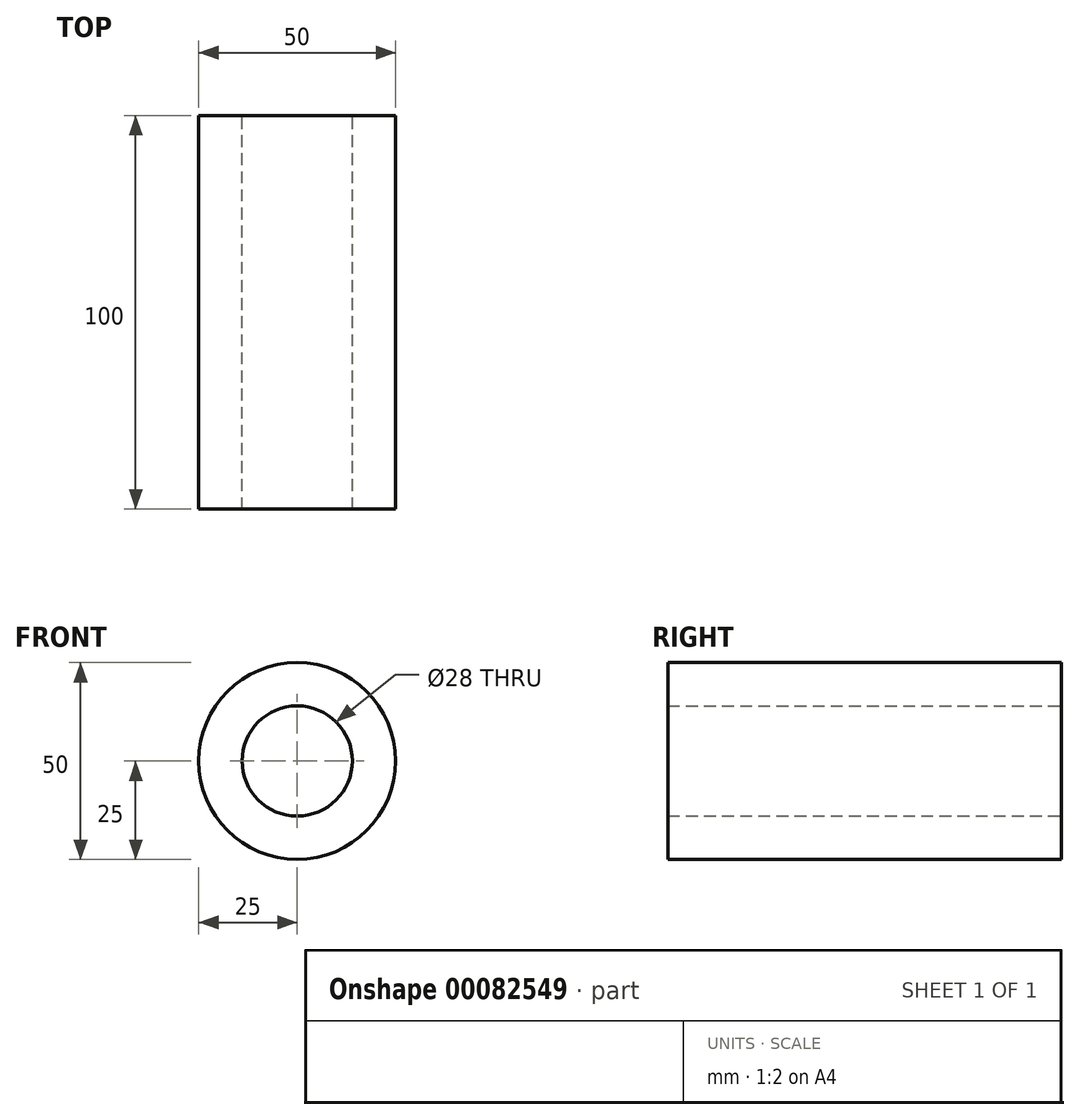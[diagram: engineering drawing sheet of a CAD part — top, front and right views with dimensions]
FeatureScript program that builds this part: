
annotation { "Feature Type Name" : "Feature", "Feature Type Description" : "" }
export const myFeature = defineFeature(function(context is Context, id is Id, definition is map)
    precondition{}
    {
        {
            var Q0;
            Q0=qCreatedBy(makeId("Front.planeOp"),FACE);
            var sketch = newSketch(context, id + "F0", { "sketchPlane" : qUnion([Q0])});
            skCircle(sketch, "E0", {"center": v(0, 0) * mm, "radius": 25 * mm});
            skCircle(sketch, "E1", {"center": v(0, 0) * mm, "radius": 14 * mm});
            skSolve(sketch);
        }
        {
            var Q0;
            Q0=makeQuery(id+"F0.imprint","IMPRINT",FACE,{"disambiguationData":[TD([[makeQuery(id+"F0.imprint","IMPRINT",EDGE,{"derivedFrom":sQuery(id+"F0.wireOp",EDGE,"E0")}),1.0]])]});
            extrude(context, id + "F1", {"entities" : qUnion([Q0]), "endBound" : BoundingType.SYMMETRIC, "depth" : 100 * mm});
        }
    });
